# Revit family: ARKOSLIGHT_Magnetic 24V Micro Shaper 52
name_source: partatom
category: Lighting Fixtures
units: mm (PartAtom-declared; Revit-internal decimal feet)

## family parameters
Cut with Voids When Loaded = No
Host = Face
Light Source = No
Part Type = Normal
Room Calculation Point = No
Round Connector Dimension = Use Diameter
Shared = No

## types (3) — shared parameters
ARKOSLIGHT_Apparent Load = 2 VA
ARKOSLIGHT_Beam Angle = 52.00°
ARKOSLIGHT_Body Color = ARKOSLIGHT_Black
ARKOSLIGHT_CRI = CRI>90
ARKOSLIGHT_Color = Black
ARKOSLIGHT_Dimming = DIM options
ARKOSLIGHT_Efficiency = 29%
ARKOSLIGHT_Fixture Type = CEILING RECESSED
ARKOSLIGHT_IP = 20
ARKOSLIGHT_Model = MAGNETIC 24V SYSTEM
ARKOSLIGHT_Series = MAGNETIC 24V MICRO SHAPER
ARKOSLIGHT_Wattage = 3 W
Apparent Load = 2 VA
Manufacturer = ARKOSLIGHT
Model = MAGNETIC 24V SYSTEM
URL = https://www.arkoslight.com
zero-valued in all types: Default Elevation

## per-type parameters (varying)
| type | ARKOSLIGHT_CCT | ARKOSLIGHT_IES | ARKOSLIGHT_Luminous flux | ARKOSLIGHT_Reference | IES |
| A5450010N - MAGNETIC 24V MICRO SHAPER 52º 2700K N | 2700 K | A545-00-10 MAGNETIC 24V MICRO SHAPER 52 2700K CRI90.ies | 190 lm | A5450010N | IES : A5450010N - MAGNETIC 24V MICRO SHAPER 52º 2700K N |
| A5450011N - MAGNETIC 24V MICRO SHAPER 52º 3000K N | 3000 K | A545-00-11 MAGNETIC 24V MICRO SHAPER 52 3000K CRI90.ies | 210 lm | A5450011N | IES : A5450011N - MAGNETIC 24V MICRO SHAPER 52º 3000K N |
| A5450012N - MAGNETIC 24V MICRO SHAPER 52º 4000K N | 4000 K | A545-00-12 MAGNETIC 24V MICRO SHAPER 52 4000K CRI90.ies | 250 lm | A5450012N | IES : A5450012N - MAGNETIC 24V MICRO SHAPER 52º 4000K N |

## geometry (parser evidence)
native form markers: Sweep x19
no freeform markers — native parametric forms only
